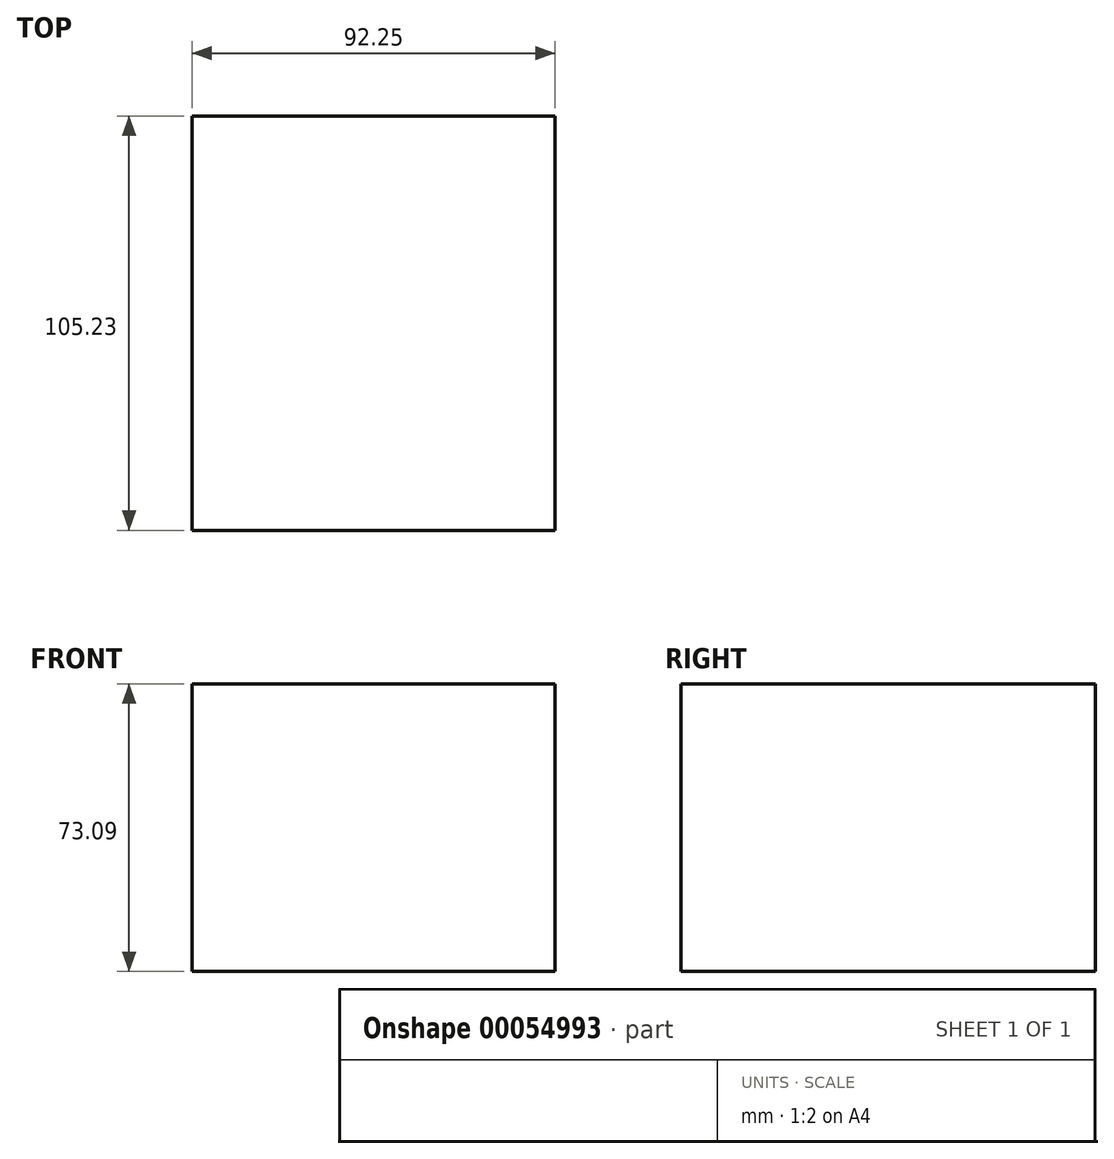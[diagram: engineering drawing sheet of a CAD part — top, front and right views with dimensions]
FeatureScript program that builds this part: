
annotation { "Feature Type Name" : "Feature", "Feature Type Description" : "" }
export const myFeature = defineFeature(function(context is Context, id is Id, definition is map)
    precondition{}
    {
        {
            var Q0;
            Q0=qCreatedBy(makeId("Front.planeOp"),FACE);
            var sketch = newSketch(context, id + "F0", { "sketchPlane" : qUnion([Q0])});
            skLineSegment(sketch, "E0.bottom", {"start": v(38.69, -31.3) * mm, "end": v(-53.56, -31.3) * mm});
            skLineSegment(sketch, "E0.top", {"start": v(38.69, 41.8) * mm, "end": v(-53.56, 41.8) * mm});
            skLineSegment(sketch, "E0.left", {"start": v(38.69, -31.3) * mm, "end": v(38.69, 41.8) * mm});
            skLineSegment(sketch, "E0.right", {"start": v(-53.56, -31.3) * mm, "end": v(-53.56, 41.8) * mm});
            skSolve(sketch);
        }
        {
            var Q0;
            Q0=makeQuery(id+"F0.imprint","IMPRINT",FACE,{"disambiguationData":[TD([[makeQuery(id+"F0.imprint","IMPRINT",EDGE,{"derivedFrom":sQuery(id+"F0.wireOp",EDGE,"E0.bottom")}),-1.0]])]});
            extrude(context, id + "F1", {"entities" : qUnion([Q0]), "depth" : 105.23 * mm});
        }
    });
